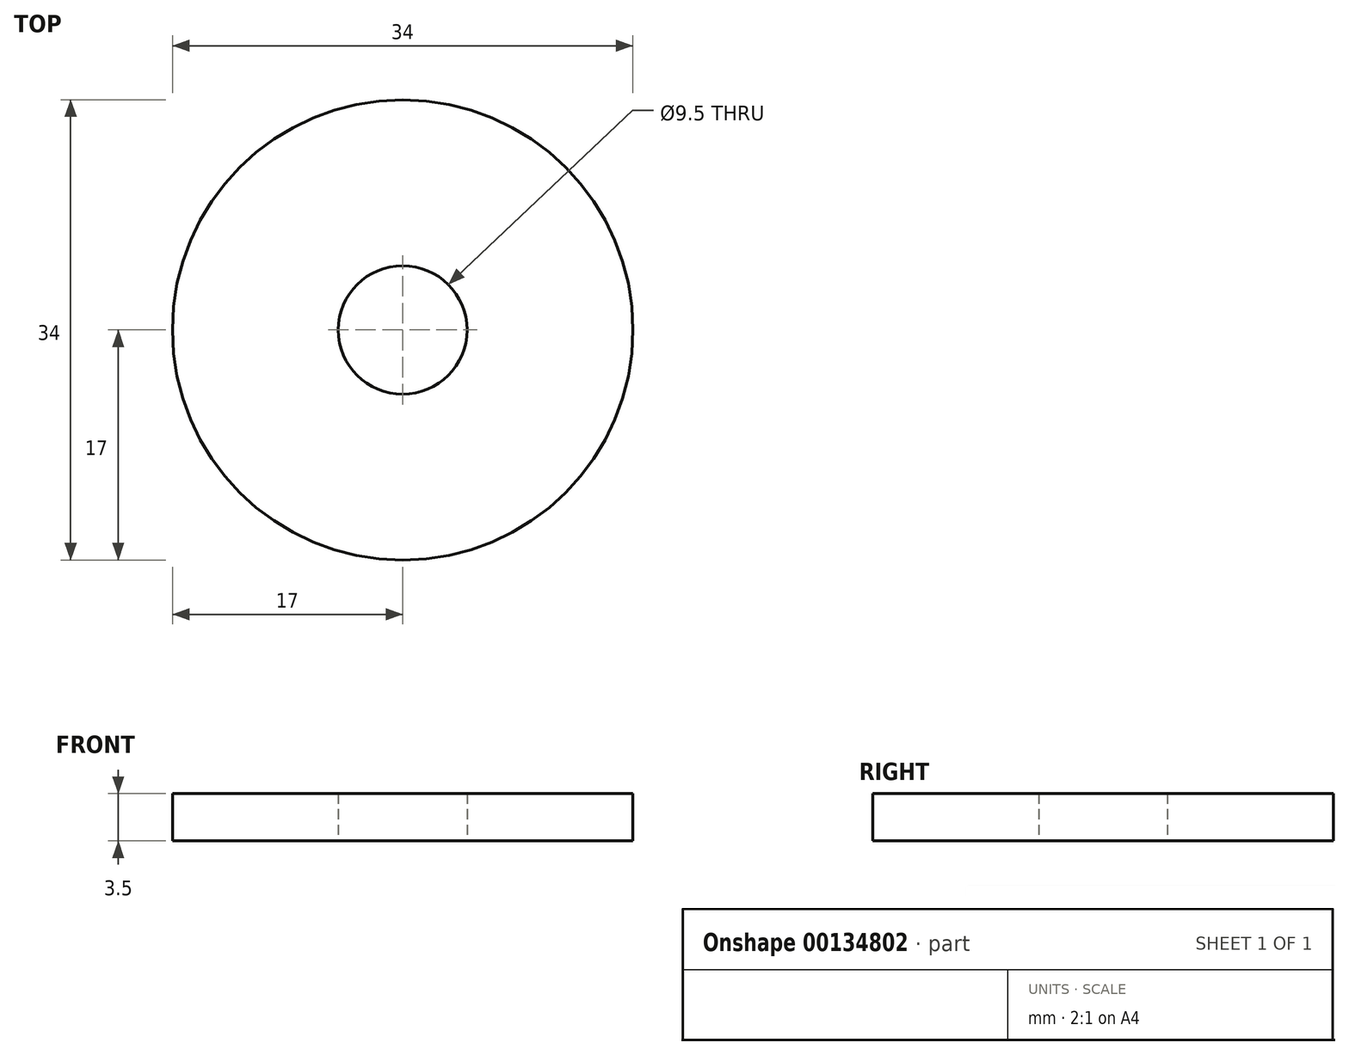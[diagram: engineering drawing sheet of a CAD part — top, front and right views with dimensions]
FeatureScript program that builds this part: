
annotation { "Feature Type Name" : "Feature", "Feature Type Description" : "" }
export const myFeature = defineFeature(function(context is Context, id is Id, definition is map)
    precondition{}
    {
        {
            var Q0;
            Q0=qCreatedBy(makeId("Top.planeOp"),FACE);
            var sketch = newSketch(context, id + "F0", { "sketchPlane" : qUnion([Q0])});
            skCircle(sketch, "E0", {"center": v(0, 0) * mm, "radius": 4.75 * mm});
            skCircle(sketch, "E1", {"center": v(0, 0) * mm, "radius": 17 * mm});
            skSolve(sketch);
        }
        {
            var Q0;
            Q0=qSketchRegion(id+"F0",true);
            extrude(context, id + "F1", {"entities" : qUnion([Q0]), "depth" : 3.5 * mm});
        }
    });
